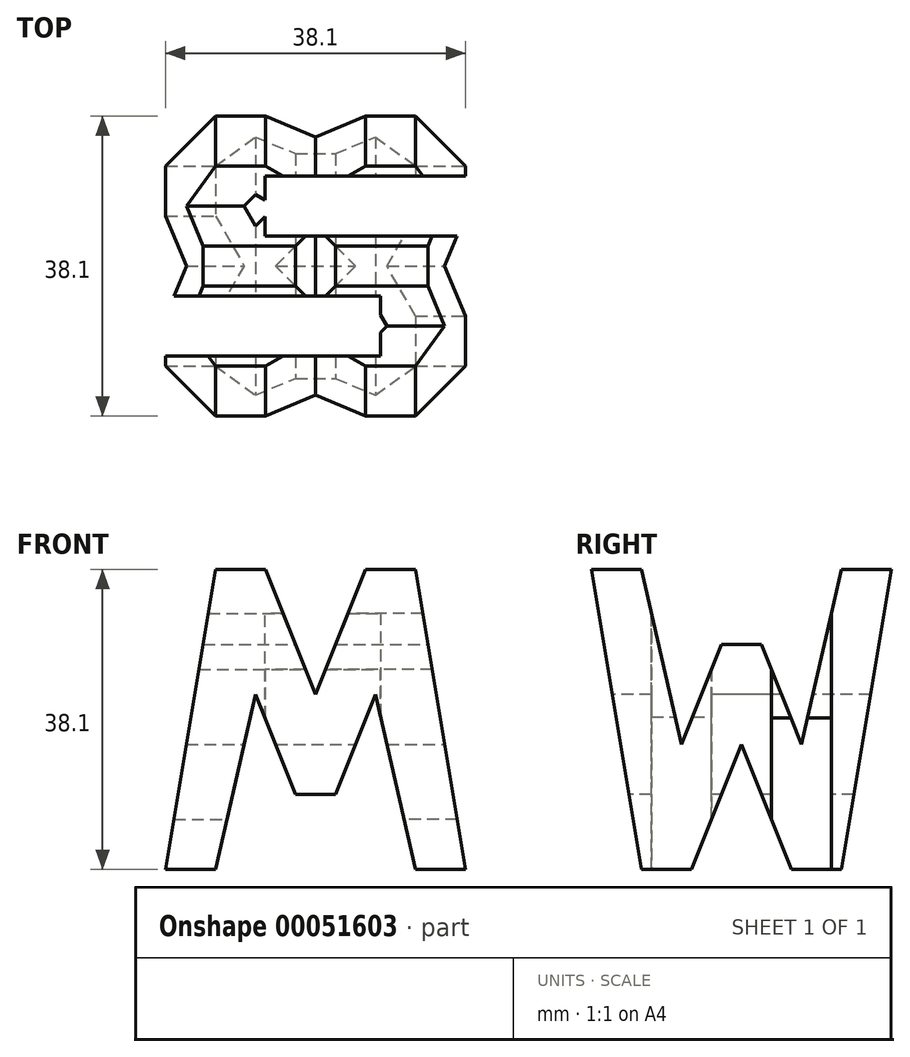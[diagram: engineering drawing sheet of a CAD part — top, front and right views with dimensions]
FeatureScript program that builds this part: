
annotation { "Feature Type Name" : "Feature", "Feature Type Description" : "" }
export const myFeature = defineFeature(function(context is Context, id is Id, definition is map)
    precondition{}
    {
        {
            var Q0;
            Q0=qCreatedBy(makeId("Front.planeOp"),FACE);
            var sketch = newSketch(context, id + "F0", { "sketchPlane" : qUnion([Q0])});
            skLineSegment(sketch, "E0", {"start": v(0, 0) * mm, "end": v(38.1, 0) * mm});
            skLineSegment(sketch, "E1", {"start": v(38.1, 0) * mm, "end": v(38.1, 38.1) * mm});
            skLineSegment(sketch, "E2", {"start": v(38.1, 38.1) * mm, "end": v(0, 38.1) * mm});
            skLineSegment(sketch, "E3", {"start": v(0, 38.1) * mm, "end": v(0, 0) * mm});
            skSolve(sketch);
        }
        {
            var Q0;
            Q0=makeQuery(id+"F0.imprint","IMPRINT",FACE,{"disambiguationData":[TD([[makeQuery(id+"F0.imprint","IMPRINT",EDGE,{"derivedFrom":sQuery(id+"F0.wireOp",EDGE,"E0")}),1.0]])]});
            extrude(context, id + "F1", {"entities" : qUnion([Q0]), "depth" : 38.1 * mm});
        }
        {
            var Q0;
            Q0=qCreatedBy(makeId("Front.planeOp"),FACE);
            cPlane(context, id + "F2", {"entities" : qUnion([Q0]), "cplaneType" : CPlaneType.OFFSET, "offset" : 38.1 * mm, "width" : 152.4 * mm, "height" : 152.4 * mm});
        }
        {
            var Q0;
            Q0=qCreatedBy(makeId("Right.planeOp"),FACE);
            cPlane(context, id + "F3", {"entities" : qUnion([Q0]), "cplaneType" : CPlaneType.OFFSET, "offset" : 38.1 * mm, "width" : 152.4 * mm, "height" : 152.4 * mm});
        }
        {
            var Q0;
            Q0=qCreatedBy(makeId("Top.planeOp"),FACE);
            cPlane(context, id + "F4", {"entities" : qUnion([Q0]), "cplaneType" : CPlaneType.OFFSET, "offset" : 38.1 * mm, "width" : 152.4 * mm, "height" : 152.4 * mm});
        }
        {
            var Q0;
            Q0=qCreatedBy(id+"F3.planeOp",FACE);
            var sketch = newSketch(context, id + "F5", { "sketchPlane" : qUnion([Q0])});
            skLineSegment(sketch, "E4.bottom", {"start": v(0, 0) * mm, "end": v(-38.1, 0) * mm});
            skLineSegment(sketch, "E4.left", {"start": v(0, 0) * mm, "end": v(0, 38.1) * mm});
            skLineSegment(sketch, "E4.right", {"start": v(-38.1, 0) * mm, "end": v(-38.1, 38.1) * mm});
            skLineSegment(sketch, "E5", {"start": v(-38.1, 38.1) * mm, "end": v(-31.75, 0) * mm});
            skLineSegment(sketch, "E6", {"start": v(-31.75, 38.1) * mm, "end": v(-26.67, 15.88) * mm});
            skLineSegment(sketch, "E7", {"start": v(-26.67, 15.88) * mm, "end": v(-21.6, 28.58) * mm});
            skLineSegment(sketch, "E8", {"start": v(-21.6, 28.58) * mm, "end": v(-16.51, 28.58) * mm});
            skLineSegment(sketch, "E9", {"start": v(-16.51, 28.58) * mm, "end": v(-11.43, 15.88) * mm});
            skLineSegment(sketch, "E10", {"start": v(-11.43, 15.88) * mm, "end": v(-6.35, 38.1) * mm});
            skLineSegment(sketch, "E11", {"start": v(0, 38.1) * mm, "end": v(-6.35, 0) * mm});
            skLineSegment(sketch, "E12", {"start": v(-25.4, 0) * mm, "end": v(-19.05, 15.88) * mm});
            skLineSegment(sketch, "E13", {"start": v(-19.05, 15.88) * mm, "end": v(-12.7, 0) * mm});
            skLineSegment(sketch, "E14", {"start": v(-38.1, 38.1) * mm, "end": v(-31.75, 38.1) * mm});
            skLineSegment(sketch, "E15", {"start": v(-6.35, 38.1) * mm, "end": v(0, 38.1) * mm});
            skLineSegment(sketch, "E16", {"start": v(-31.75, 38.1) * mm, "end": v(-6.35, 38.1) * mm});
            skSolve(sketch);
        }
        {
            var Q0;
            Q0=makeQuery(id+"F5.imprint","IMPRINT",FACE,{"disambiguationData":[TD([[makeQuery(id+"F5.imprint","IMPRINT",EDGE,{"derivedFrom":sQuery(id+"F5.wireOp",EDGE,"E6")}),1.0]])]});
            var Q1;
            {var subQ0=sQuery(id+"F5.wireOp",EDGE,"E12");Q1=makeQuery(id+"F5.imprint","IMPRINT",FACE,{"disambiguationData":[TD([[makeQuery(id+"F5.imprint","IMPRINT",EDGE,{"derivedFrom":subQ0}),-1.0]])]});}
            var Q2;
            {var subQ0=sQuery(id+"F5.wireOp",EDGE,"E4.right");Q2=makeQuery(id+"F5.imprint","IMPRINT",FACE,{"disambiguationData":[TD([[makeQuery(id+"F5.imprint","IMPRINT",EDGE,{"derivedFrom":subQ0}),-1.0]])]});}
            var Q3;
            {var subQ0=sQuery(id+"F5.wireOp",EDGE,"E4.left");Q3=makeQuery(id+"F5.imprint","IMPRINT",FACE,{"disambiguationData":[TD([[makeQuery(id+"F5.imprint","IMPRINT",EDGE,{"derivedFrom":subQ0}),1.0]])]});}
            extrude(context, id + "F6", {"entities" : qUnion([Q0, Q1, Q2, Q3]), "operationType" : NewBodyOperationType.REMOVE, "oppositeDirection" : true, "depth" : 38.1 * mm});
        }
        {
            var Q0;
            Q0=qCreatedBy(id+"F2.planeOp",FACE);
            var sketch = newSketch(context, id + "F7", { "sketchPlane" : qUnion([Q0])});
            skLineSegment(sketch, "E17", {"start": v(0, 0) * mm, "end": v(38.1, 0) * mm});
            skLineSegment(sketch, "E18", {"start": v(38.1, 0) * mm, "end": v(38.1, 38.1) * mm});
            skLineSegment(sketch, "E19", {"start": v(38.1, 38.1) * mm, "end": v(0, 38.1) * mm});
            skLineSegment(sketch, "E20", {"start": v(0, 38.1) * mm, "end": v(0, 0) * mm});
            skLineSegment(sketch, "E21", {"start": v(6.35, 38.1) * mm, "end": v(0, 0) * mm});
            skLineSegment(sketch, "E22", {"start": v(6.35, 0) * mm, "end": v(11.43, 22.23) * mm});
            skLineSegment(sketch, "E23", {"start": v(11.43, 22.23) * mm, "end": v(16.51, 9.53) * mm});
            skLineSegment(sketch, "E24", {"start": v(16.51, 9.53) * mm, "end": v(21.6, 9.53) * mm});
            skLineSegment(sketch, "E25", {"start": v(21.6, 9.53) * mm, "end": v(26.67, 22.22) * mm});
            skLineSegment(sketch, "E26", {"start": v(26.67, 22.23) * mm, "end": v(31.75, 0) * mm});
            skLineSegment(sketch, "E27", {"start": v(38.1, 0) * mm, "end": v(31.75, 38.1) * mm});
            skLineSegment(sketch, "E28", {"start": v(25.4, 38.1) * mm, "end": v(19.05, 22.23) * mm});
            skLineSegment(sketch, "E29", {"start": v(19.05, 22.23) * mm, "end": v(12.7, 38.1) * mm});
            skLineSegment(sketch, "E30", {"start": v(0, 38.1) * mm, "end": v(38.1, 38.1) * mm});
            skSolve(sketch);
        }
        {
            var Q0;
            {var subQ0=sQuery(id+"F7.wireOp",EDGE,"E28");Q0=makeQuery(id+"F7.imprint","IMPRINT",FACE,{"disambiguationData":[TD([[makeQuery(id+"F7.imprint","IMPRINT",EDGE,{"derivedFrom":subQ0}),-1.0]])]});}
            var Q1;
            {var subQ0=sQuery(id+"F7.wireOp",EDGE,"E22");Q1=makeQuery(id+"F7.imprint","IMPRINT",FACE,{"disambiguationData":[TD([[makeQuery(id+"F7.imprint","IMPRINT",EDGE,{"derivedFrom":subQ0}),-1.0]])]});}
            var Q2;
            {var subQ0=sQuery(id+"F7.wireOp",EDGE,"E20");Q2=makeQuery(id+"F7.imprint","IMPRINT",FACE,{"disambiguationData":[TD([[makeQuery(id+"F7.imprint","IMPRINT",EDGE,{"derivedFrom":subQ0}),1.0]])]});}
            var Q3;
            {var subQ0=sQuery(id+"F7.wireOp",EDGE,"E18");Q3=makeQuery(id+"F7.imprint","IMPRINT",FACE,{"disambiguationData":[TD([[makeQuery(id+"F7.imprint","IMPRINT",EDGE,{"derivedFrom":subQ0}),1.0]])]});}
            extrude(context, id + "F8", {"entities" : qUnion([Q0, Q1, Q2, Q3]), "operationType" : NewBodyOperationType.REMOVE, "oppositeDirection" : true, "depth" : 38.1 * mm});
        }
        {
            var Q0;
            Q0=qCreatedBy(id+"F4.planeOp",FACE);
            var sketch = newSketch(context, id + "F9", { "sketchPlane" : qUnion([Q0])});
            skLineSegment(sketch, "E31", {"start": v(0, 0) * mm, "end": v(38.1, 0) * mm});
            skLineSegment(sketch, "E32", {"start": v(38.1, 0) * mm, "end": v(38.1, -38.1) * mm});
            skLineSegment(sketch, "E33", {"start": v(38.1, -38.1) * mm, "end": v(0, -38.1) * mm});
            skLineSegment(sketch, "E34", {"start": v(0, -38.1) * mm, "end": v(0, 0) * mm});
            skLineSegment(sketch, "E35", {"start": v(12.61, -7.62) * mm, "end": v(38.1, -7.62) * mm});
            skLineSegment(sketch, "E36", {"start": v(12.61, -7.62) * mm, "end": v(12.61, -15.24) * mm});
            skLineSegment(sketch, "E37", {"start": v(12.61, -15.24) * mm, "end": v(38.1, -15.24) * mm});
            skLineSegment(sketch, "E38", {"start": v(27.32, -22.86) * mm, "end": v(0, -22.86) * mm});
            skLineSegment(sketch, "E39", {"start": v(27.32, -22.86) * mm, "end": v(27.32, -30.48) * mm});
            skLineSegment(sketch, "E40", {"start": v(27.32, -30.48) * mm, "end": v(0, -30.48) * mm});
            skSolve(sketch);
        }
        {
            var Q0;
            {var subQ0=sQuery(id+"F9.wireOp",EDGE,"E35");Q0=makeQuery(id+"F9.imprint","IMPRINT",FACE,{"disambiguationData":[TD([[makeQuery(id+"F9.imprint","IMPRINT",EDGE,{"derivedFrom":subQ0}),-1.0]])]});}
            var Q1;
            {var subQ0=sQuery(id+"F9.wireOp",EDGE,"E38");Q1=makeQuery(id+"F9.imprint","IMPRINT",FACE,{"disambiguationData":[TD([[makeQuery(id+"F9.imprint","IMPRINT",EDGE,{"derivedFrom":subQ0}),1.0]])]});}
            extrude(context, id + "F10", {"entities" : qUnion([Q0, Q1]), "operationType" : NewBodyOperationType.REMOVE, "oppositeDirection" : true, "depth" : 38.1 * mm});
        }
    });
